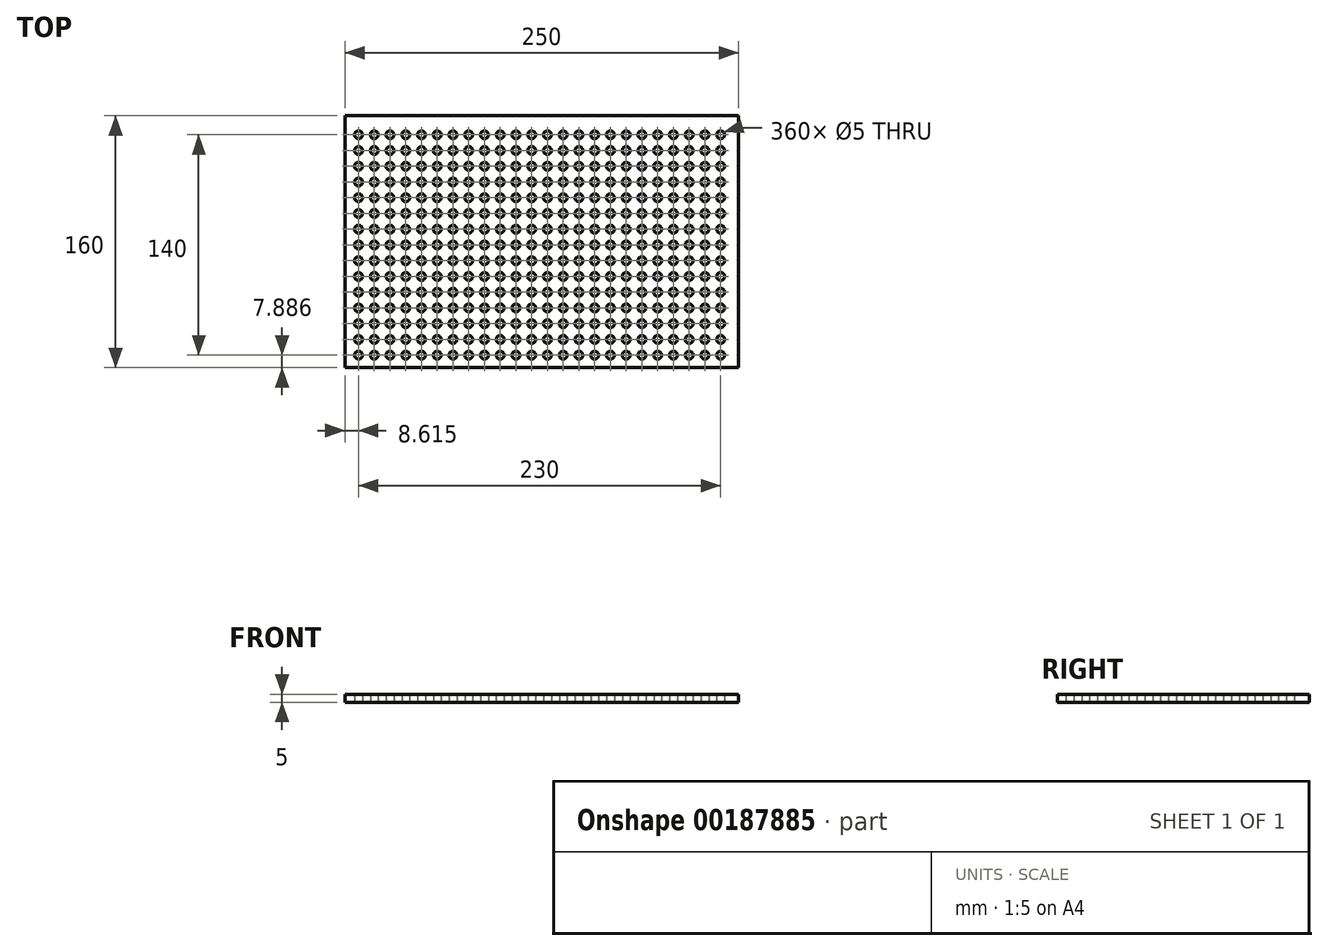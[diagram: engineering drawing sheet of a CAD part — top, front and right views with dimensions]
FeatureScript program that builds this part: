
annotation { "Feature Type Name" : "Feature", "Feature Type Description" : "" }
export const myFeature = defineFeature(function(context is Context, id is Id, definition is map)
    precondition{}
    {
        {
            var Q0;
            Q0=qCreatedBy(makeId("Top.planeOp"),FACE);
            var sketch = newSketch(context, id + "F0", { "sketchPlane" : qUnion([Q0])});
            skLineSegment(sketch, "E0.bottom", {"start": v(125, -80) * mm, "end": v(-125, -80) * mm});
            skLineSegment(sketch, "E0.top", {"start": v(125, 80) * mm, "end": v(-125, 80) * mm});
            skLineSegment(sketch, "E0.left", {"start": v(125, -80) * mm, "end": v(125, 80) * mm});
            skLineSegment(sketch, "E0.right", {"start": v(-125, -80) * mm, "end": v(-125, 80) * mm});
            skPoint(sketch, "E0.middle", {"position": v(0, 0) * mm});
            skCircle(sketch, "E1", {"center": v(-116.38, -72.11) * mm, "radius": 2.5 * mm});
            skCircle(sketch, "E2.0.1.0", {"center": v(-116.38, -62.11) * mm, "radius": 2.5 * mm});
            skCircle(sketch, "E2.0.2.0", {"center": v(-116.38, -52.11) * mm, "radius": 2.5 * mm});
            skCircle(sketch, "E2.0.3.0", {"center": v(-116.38, -42.11) * mm, "radius": 2.5 * mm});
            skCircle(sketch, "E2.0.4.0", {"center": v(-116.38, -32.11) * mm, "radius": 2.5 * mm});
            skCircle(sketch, "E2.0.5.0", {"center": v(-116.38, -22.11) * mm, "radius": 2.5 * mm});
            skCircle(sketch, "E2.0.6.0", {"center": v(-116.38, -12.11) * mm, "radius": 2.5 * mm});
            skCircle(sketch, "E2.0.7.0", {"center": v(-116.38, -2.11) * mm, "radius": 2.5 * mm});
            skCircle(sketch, "E2.0.8.0", {"center": v(-116.38, 7.89) * mm, "radius": 2.5 * mm});
            skCircle(sketch, "E2.0.9.0", {"center": v(-116.38, 17.89) * mm, "radius": 2.5 * mm});
            skCircle(sketch, "E2.0.10.0", {"center": v(-116.38, 27.89) * mm, "radius": 2.5 * mm});
            skCircle(sketch, "E2.0.11.0", {"center": v(-116.38, 37.89) * mm, "radius": 2.5 * mm});
            skCircle(sketch, "E2.0.12.0", {"center": v(-116.38, 47.89) * mm, "radius": 2.5 * mm});
            skCircle(sketch, "E2.0.13.0", {"center": v(-116.38, 57.89) * mm, "radius": 2.5 * mm});
            skCircle(sketch, "E2.0.14.0", {"center": v(-116.38, 67.89) * mm, "radius": 2.5 * mm});
            skCircle(sketch, "E2.1.0.0", {"center": v(-106.38, -72.11) * mm, "radius": 2.5 * mm});
            skCircle(sketch, "E2.1.1.0", {"center": v(-106.38, -62.11) * mm, "radius": 2.5 * mm});
            skCircle(sketch, "E2.1.2.0", {"center": v(-106.38, -52.11) * mm, "radius": 2.5 * mm});
            skCircle(sketch, "E2.1.3.0", {"center": v(-106.38, -42.11) * mm, "radius": 2.5 * mm});
            skCircle(sketch, "E2.1.4.0", {"center": v(-106.38, -32.11) * mm, "radius": 2.5 * mm});
            skCircle(sketch, "E2.1.5.0", {"center": v(-106.38, -22.11) * mm, "radius": 2.5 * mm});
            skCircle(sketch, "E2.1.6.0", {"center": v(-106.38, -12.11) * mm, "radius": 2.5 * mm});
            skCircle(sketch, "E2.1.7.0", {"center": v(-106.38, -2.11) * mm, "radius": 2.5 * mm});
            skCircle(sketch, "E2.1.8.0", {"center": v(-106.38, 7.89) * mm, "radius": 2.5 * mm});
            skCircle(sketch, "E2.1.9.0", {"center": v(-106.38, 17.89) * mm, "radius": 2.5 * mm});
            skCircle(sketch, "E2.1.10.0", {"center": v(-106.38, 27.89) * mm, "radius": 2.5 * mm});
            skCircle(sketch, "E2.1.11.0", {"center": v(-106.38, 37.89) * mm, "radius": 2.5 * mm});
            skCircle(sketch, "E2.1.12.0", {"center": v(-106.38, 47.89) * mm, "radius": 2.5 * mm});
            skCircle(sketch, "E2.1.13.0", {"center": v(-106.38, 57.89) * mm, "radius": 2.5 * mm});
            skCircle(sketch, "E2.1.14.0", {"center": v(-106.38, 67.89) * mm, "radius": 2.5 * mm});
            skCircle(sketch, "E2.2.0.0", {"center": v(-96.38, -72.11) * mm, "radius": 2.5 * mm});
            skCircle(sketch, "E2.2.1.0", {"center": v(-96.38, -62.11) * mm, "radius": 2.5 * mm});
            skCircle(sketch, "E2.2.2.0", {"center": v(-96.38, -52.11) * mm, "radius": 2.5 * mm});
            skCircle(sketch, "E2.2.3.0", {"center": v(-96.38, -42.11) * mm, "radius": 2.5 * mm});
            skCircle(sketch, "E2.2.4.0", {"center": v(-96.38, -32.11) * mm, "radius": 2.5 * mm});
            skCircle(sketch, "E2.2.5.0", {"center": v(-96.38, -22.11) * mm, "radius": 2.5 * mm});
            skCircle(sketch, "E2.2.6.0", {"center": v(-96.38, -12.11) * mm, "radius": 2.5 * mm});
            skCircle(sketch, "E2.2.7.0", {"center": v(-96.38, -2.11) * mm, "radius": 2.5 * mm});
            skCircle(sketch, "E2.2.8.0", {"center": v(-96.38, 7.89) * mm, "radius": 2.5 * mm});
            skCircle(sketch, "E2.2.9.0", {"center": v(-96.38, 17.89) * mm, "radius": 2.5 * mm});
            skCircle(sketch, "E2.2.10.0", {"center": v(-96.38, 27.89) * mm, "radius": 2.5 * mm});
            skCircle(sketch, "E2.2.11.0", {"center": v(-96.38, 37.89) * mm, "radius": 2.5 * mm});
            skCircle(sketch, "E2.2.12.0", {"center": v(-96.38, 47.89) * mm, "radius": 2.5 * mm});
            skCircle(sketch, "E2.2.13.0", {"center": v(-96.38, 57.89) * mm, "radius": 2.5 * mm});
            skCircle(sketch, "E2.2.14.0", {"center": v(-96.38, 67.89) * mm, "radius": 2.5 * mm});
            skCircle(sketch, "E2.3.0.0", {"center": v(-86.38, -72.11) * mm, "radius": 2.5 * mm});
            skCircle(sketch, "E2.3.1.0", {"center": v(-86.38, -62.11) * mm, "radius": 2.5 * mm});
            skCircle(sketch, "E2.3.2.0", {"center": v(-86.38, -52.11) * mm, "radius": 2.5 * mm});
            skCircle(sketch, "E2.3.3.0", {"center": v(-86.38, -42.11) * mm, "radius": 2.5 * mm});
            skCircle(sketch, "E2.3.4.0", {"center": v(-86.38, -32.11) * mm, "radius": 2.5 * mm});
            skCircle(sketch, "E2.3.5.0", {"center": v(-86.38, -22.11) * mm, "radius": 2.5 * mm});
            skCircle(sketch, "E2.3.6.0", {"center": v(-86.38, -12.11) * mm, "radius": 2.5 * mm});
            skCircle(sketch, "E2.3.7.0", {"center": v(-86.38, -2.11) * mm, "radius": 2.5 * mm});
            skCircle(sketch, "E2.3.8.0", {"center": v(-86.38, 7.89) * mm, "radius": 2.5 * mm});
            skCircle(sketch, "E2.3.9.0", {"center": v(-86.38, 17.89) * mm, "radius": 2.5 * mm});
            skCircle(sketch, "E2.3.10.0", {"center": v(-86.38, 27.89) * mm, "radius": 2.5 * mm});
            skCircle(sketch, "E2.3.11.0", {"center": v(-86.38, 37.89) * mm, "radius": 2.5 * mm});
            skCircle(sketch, "E2.3.12.0", {"center": v(-86.38, 47.89) * mm, "radius": 2.5 * mm});
            skCircle(sketch, "E2.3.13.0", {"center": v(-86.38, 57.89) * mm, "radius": 2.5 * mm});
            skCircle(sketch, "E2.3.14.0", {"center": v(-86.38, 67.89) * mm, "radius": 2.5 * mm});
            skCircle(sketch, "E2.4.0.0", {"center": v(-76.38, -72.11) * mm, "radius": 2.5 * mm});
            skCircle(sketch, "E2.4.1.0", {"center": v(-76.38, -62.11) * mm, "radius": 2.5 * mm});
            skCircle(sketch, "E2.4.2.0", {"center": v(-76.38, -52.11) * mm, "radius": 2.5 * mm});
            skCircle(sketch, "E2.4.3.0", {"center": v(-76.38, -42.11) * mm, "radius": 2.5 * mm});
            skCircle(sketch, "E2.4.4.0", {"center": v(-76.38, -32.11) * mm, "radius": 2.5 * mm});
            skCircle(sketch, "E2.4.5.0", {"center": v(-76.38, -22.11) * mm, "radius": 2.5 * mm});
            skCircle(sketch, "E2.4.6.0", {"center": v(-76.38, -12.11) * mm, "radius": 2.5 * mm});
            skCircle(sketch, "E2.4.7.0", {"center": v(-76.38, -2.11) * mm, "radius": 2.5 * mm});
            skCircle(sketch, "E2.4.8.0", {"center": v(-76.38, 7.89) * mm, "radius": 2.5 * mm});
            skCircle(sketch, "E2.4.9.0", {"center": v(-76.38, 17.89) * mm, "radius": 2.5 * mm});
            skCircle(sketch, "E2.4.10.0", {"center": v(-76.38, 27.89) * mm, "radius": 2.5 * mm});
            skCircle(sketch, "E2.4.11.0", {"center": v(-76.38, 37.89) * mm, "radius": 2.5 * mm});
            skCircle(sketch, "E2.4.12.0", {"center": v(-76.38, 47.89) * mm, "radius": 2.5 * mm});
            skCircle(sketch, "E2.4.13.0", {"center": v(-76.38, 57.89) * mm, "radius": 2.5 * mm});
            skCircle(sketch, "E2.4.14.0", {"center": v(-76.38, 67.89) * mm, "radius": 2.5 * mm});
            skCircle(sketch, "E2.5.0.0", {"center": v(-66.38, -72.11) * mm, "radius": 2.5 * mm});
            skCircle(sketch, "E2.5.1.0", {"center": v(-66.38, -62.11) * mm, "radius": 2.5 * mm});
            skCircle(sketch, "E2.5.2.0", {"center": v(-66.38, -52.11) * mm, "radius": 2.5 * mm});
            skCircle(sketch, "E2.5.3.0", {"center": v(-66.38, -42.11) * mm, "radius": 2.5 * mm});
            skCircle(sketch, "E2.5.4.0", {"center": v(-66.38, -32.11) * mm, "radius": 2.5 * mm});
            skCircle(sketch, "E2.5.5.0", {"center": v(-66.38, -22.11) * mm, "radius": 2.5 * mm});
            skCircle(sketch, "E2.5.6.0", {"center": v(-66.38, -12.11) * mm, "radius": 2.5 * mm});
            skCircle(sketch, "E2.5.7.0", {"center": v(-66.38, -2.11) * mm, "radius": 2.5 * mm});
            skCircle(sketch, "E2.5.8.0", {"center": v(-66.38, 7.89) * mm, "radius": 2.5 * mm});
            skCircle(sketch, "E2.5.9.0", {"center": v(-66.38, 17.89) * mm, "radius": 2.5 * mm});
            skCircle(sketch, "E2.5.10.0", {"center": v(-66.38, 27.89) * mm, "radius": 2.5 * mm});
            skCircle(sketch, "E2.5.11.0", {"center": v(-66.38, 37.89) * mm, "radius": 2.5 * mm});
            skCircle(sketch, "E2.5.12.0", {"center": v(-66.38, 47.89) * mm, "radius": 2.5 * mm});
            skCircle(sketch, "E2.5.13.0", {"center": v(-66.38, 57.89) * mm, "radius": 2.5 * mm});
            skCircle(sketch, "E2.5.14.0", {"center": v(-66.38, 67.89) * mm, "radius": 2.5 * mm});
            skCircle(sketch, "E2.6.0.0", {"center": v(-56.38, -72.11) * mm, "radius": 2.5 * mm});
            skCircle(sketch, "E2.6.1.0", {"center": v(-56.38, -62.11) * mm, "radius": 2.5 * mm});
            skCircle(sketch, "E2.6.2.0", {"center": v(-56.38, -52.11) * mm, "radius": 2.5 * mm});
            skCircle(sketch, "E2.6.3.0", {"center": v(-56.38, -42.11) * mm, "radius": 2.5 * mm});
            skCircle(sketch, "E2.6.4.0", {"center": v(-56.38, -32.11) * mm, "radius": 2.5 * mm});
            skCircle(sketch, "E2.6.5.0", {"center": v(-56.38, -22.11) * mm, "radius": 2.5 * mm});
            skCircle(sketch, "E2.6.6.0", {"center": v(-56.38, -12.11) * mm, "radius": 2.5 * mm});
            skCircle(sketch, "E2.6.7.0", {"center": v(-56.38, -2.11) * mm, "radius": 2.5 * mm});
            skCircle(sketch, "E2.6.8.0", {"center": v(-56.38, 7.89) * mm, "radius": 2.5 * mm});
            skCircle(sketch, "E2.6.9.0", {"center": v(-56.38, 17.89) * mm, "radius": 2.5 * mm});
            skCircle(sketch, "E2.6.10.0", {"center": v(-56.38, 27.89) * mm, "radius": 2.5 * mm});
            skCircle(sketch, "E2.6.11.0", {"center": v(-56.38, 37.89) * mm, "radius": 2.5 * mm});
            skCircle(sketch, "E2.6.12.0", {"center": v(-56.38, 47.89) * mm, "radius": 2.5 * mm});
            skCircle(sketch, "E2.6.13.0", {"center": v(-56.38, 57.89) * mm, "radius": 2.5 * mm});
            skCircle(sketch, "E2.6.14.0", {"center": v(-56.38, 67.89) * mm, "radius": 2.5 * mm});
            skCircle(sketch, "E2.7.0.0", {"center": v(-46.38, -72.11) * mm, "radius": 2.5 * mm});
            skCircle(sketch, "E2.7.1.0", {"center": v(-46.38, -62.11) * mm, "radius": 2.5 * mm});
            skCircle(sketch, "E2.7.2.0", {"center": v(-46.38, -52.11) * mm, "radius": 2.5 * mm});
            skCircle(sketch, "E2.7.3.0", {"center": v(-46.38, -42.11) * mm, "radius": 2.5 * mm});
            skCircle(sketch, "E2.7.4.0", {"center": v(-46.38, -32.11) * mm, "radius": 2.5 * mm});
            skCircle(sketch, "E2.7.5.0", {"center": v(-46.38, -22.11) * mm, "radius": 2.5 * mm});
            skCircle(sketch, "E2.7.6.0", {"center": v(-46.38, -12.11) * mm, "radius": 2.5 * mm});
            skCircle(sketch, "E2.7.7.0", {"center": v(-46.38, -2.11) * mm, "radius": 2.5 * mm});
            skCircle(sketch, "E2.7.8.0", {"center": v(-46.38, 7.89) * mm, "radius": 2.5 * mm});
            skCircle(sketch, "E2.7.9.0", {"center": v(-46.38, 17.89) * mm, "radius": 2.5 * mm});
            skCircle(sketch, "E2.7.10.0", {"center": v(-46.38, 27.89) * mm, "radius": 2.5 * mm});
            skCircle(sketch, "E2.7.11.0", {"center": v(-46.38, 37.89) * mm, "radius": 2.5 * mm});
            skCircle(sketch, "E2.7.12.0", {"center": v(-46.38, 47.89) * mm, "radius": 2.5 * mm});
            skCircle(sketch, "E2.7.13.0", {"center": v(-46.38, 57.89) * mm, "radius": 2.5 * mm});
            skCircle(sketch, "E2.7.14.0", {"center": v(-46.38, 67.89) * mm, "radius": 2.5 * mm});
            skCircle(sketch, "E2.8.0.0", {"center": v(-36.38, -72.11) * mm, "radius": 2.5 * mm});
            skCircle(sketch, "E2.8.1.0", {"center": v(-36.38, -62.11) * mm, "radius": 2.5 * mm});
            skCircle(sketch, "E2.8.2.0", {"center": v(-36.38, -52.11) * mm, "radius": 2.5 * mm});
            skCircle(sketch, "E2.8.3.0", {"center": v(-36.38, -42.11) * mm, "radius": 2.5 * mm});
            skCircle(sketch, "E2.8.4.0", {"center": v(-36.38, -32.11) * mm, "radius": 2.5 * mm});
            skCircle(sketch, "E2.8.5.0", {"center": v(-36.38, -22.11) * mm, "radius": 2.5 * mm});
            skCircle(sketch, "E2.8.6.0", {"center": v(-36.38, -12.11) * mm, "radius": 2.5 * mm});
            skCircle(sketch, "E2.8.7.0", {"center": v(-36.38, -2.11) * mm, "radius": 2.5 * mm});
            skCircle(sketch, "E2.8.8.0", {"center": v(-36.38, 7.89) * mm, "radius": 2.5 * mm});
            skCircle(sketch, "E2.8.9.0", {"center": v(-36.38, 17.89) * mm, "radius": 2.5 * mm});
            skCircle(sketch, "E2.8.10.0", {"center": v(-36.38, 27.89) * mm, "radius": 2.5 * mm});
            skCircle(sketch, "E2.8.11.0", {"center": v(-36.38, 37.89) * mm, "radius": 2.5 * mm});
            skCircle(sketch, "E2.8.12.0", {"center": v(-36.38, 47.89) * mm, "radius": 2.5 * mm});
            skCircle(sketch, "E2.8.13.0", {"center": v(-36.38, 57.89) * mm, "radius": 2.5 * mm});
            skCircle(sketch, "E2.8.14.0", {"center": v(-36.38, 67.89) * mm, "radius": 2.5 * mm});
            skCircle(sketch, "E2.9.0.0", {"center": v(-26.38, -72.11) * mm, "radius": 2.5 * mm});
            skCircle(sketch, "E2.9.1.0", {"center": v(-26.38, -62.11) * mm, "radius": 2.5 * mm});
            skCircle(sketch, "E2.9.2.0", {"center": v(-26.38, -52.11) * mm, "radius": 2.5 * mm});
            skCircle(sketch, "E2.9.3.0", {"center": v(-26.38, -42.11) * mm, "radius": 2.5 * mm});
            skCircle(sketch, "E2.9.4.0", {"center": v(-26.38, -32.11) * mm, "radius": 2.5 * mm});
            skCircle(sketch, "E2.9.5.0", {"center": v(-26.38, -22.11) * mm, "radius": 2.5 * mm});
            skCircle(sketch, "E2.9.6.0", {"center": v(-26.38, -12.11) * mm, "radius": 2.5 * mm});
            skCircle(sketch, "E2.9.7.0", {"center": v(-26.38, -2.11) * mm, "radius": 2.5 * mm});
            skCircle(sketch, "E2.9.8.0", {"center": v(-26.38, 7.89) * mm, "radius": 2.5 * mm});
            skCircle(sketch, "E2.9.9.0", {"center": v(-26.38, 17.89) * mm, "radius": 2.5 * mm});
            skCircle(sketch, "E2.9.10.0", {"center": v(-26.38, 27.89) * mm, "radius": 2.5 * mm});
            skCircle(sketch, "E2.9.11.0", {"center": v(-26.38, 37.89) * mm, "radius": 2.5 * mm});
            skCircle(sketch, "E2.9.12.0", {"center": v(-26.38, 47.89) * mm, "radius": 2.5 * mm});
            skCircle(sketch, "E2.9.13.0", {"center": v(-26.38, 57.89) * mm, "radius": 2.5 * mm});
            skCircle(sketch, "E2.9.14.0", {"center": v(-26.38, 67.89) * mm, "radius": 2.5 * mm});
            skCircle(sketch, "E2.10.0.0", {"center": v(-16.38, -72.11) * mm, "radius": 2.5 * mm});
            skCircle(sketch, "E2.10.1.0", {"center": v(-16.38, -62.11) * mm, "radius": 2.5 * mm});
            skCircle(sketch, "E2.10.2.0", {"center": v(-16.38, -52.11) * mm, "radius": 2.5 * mm});
            skCircle(sketch, "E2.10.3.0", {"center": v(-16.38, -42.11) * mm, "radius": 2.5 * mm});
            skCircle(sketch, "E2.10.4.0", {"center": v(-16.38, -32.11) * mm, "radius": 2.5 * mm});
            skCircle(sketch, "E2.10.5.0", {"center": v(-16.38, -22.11) * mm, "radius": 2.5 * mm});
            skCircle(sketch, "E2.10.6.0", {"center": v(-16.38, -12.11) * mm, "radius": 2.5 * mm});
            skCircle(sketch, "E2.10.7.0", {"center": v(-16.38, -2.11) * mm, "radius": 2.5 * mm});
            skCircle(sketch, "E2.10.8.0", {"center": v(-16.38, 7.89) * mm, "radius": 2.5 * mm});
            skCircle(sketch, "E2.10.9.0", {"center": v(-16.38, 17.89) * mm, "radius": 2.5 * mm});
            skCircle(sketch, "E2.10.10.0", {"center": v(-16.38, 27.89) * mm, "radius": 2.5 * mm});
            skCircle(sketch, "E2.10.11.0", {"center": v(-16.38, 37.89) * mm, "radius": 2.5 * mm});
            skCircle(sketch, "E2.10.12.0", {"center": v(-16.38, 47.89) * mm, "radius": 2.5 * mm});
            skCircle(sketch, "E2.10.13.0", {"center": v(-16.38, 57.89) * mm, "radius": 2.5 * mm});
            skCircle(sketch, "E2.10.14.0", {"center": v(-16.38, 67.89) * mm, "radius": 2.5 * mm});
            skCircle(sketch, "E2.11.0.0", {"center": v(-6.38, -72.11) * mm, "radius": 2.5 * mm});
            skCircle(sketch, "E2.11.1.0", {"center": v(-6.38, -62.11) * mm, "radius": 2.5 * mm});
            skCircle(sketch, "E2.11.2.0", {"center": v(-6.38, -52.11) * mm, "radius": 2.5 * mm});
            skCircle(sketch, "E2.11.3.0", {"center": v(-6.38, -42.11) * mm, "radius": 2.5 * mm});
            skCircle(sketch, "E2.11.4.0", {"center": v(-6.38, -32.11) * mm, "radius": 2.5 * mm});
            skCircle(sketch, "E2.11.5.0", {"center": v(-6.38, -22.11) * mm, "radius": 2.5 * mm});
            skCircle(sketch, "E2.11.6.0", {"center": v(-6.38, -12.11) * mm, "radius": 2.5 * mm});
            skCircle(sketch, "E2.11.7.0", {"center": v(-6.38, -2.11) * mm, "radius": 2.5 * mm});
            skCircle(sketch, "E2.11.8.0", {"center": v(-6.38, 7.89) * mm, "radius": 2.5 * mm});
            skCircle(sketch, "E2.11.9.0", {"center": v(-6.38, 17.89) * mm, "radius": 2.5 * mm});
            skCircle(sketch, "E2.11.10.0", {"center": v(-6.38, 27.89) * mm, "radius": 2.5 * mm});
            skCircle(sketch, "E2.11.11.0", {"center": v(-6.38, 37.89) * mm, "radius": 2.5 * mm});
            skCircle(sketch, "E2.11.12.0", {"center": v(-6.38, 47.89) * mm, "radius": 2.5 * mm});
            skCircle(sketch, "E2.11.13.0", {"center": v(-6.38, 57.89) * mm, "radius": 2.5 * mm});
            skCircle(sketch, "E2.11.14.0", {"center": v(-6.38, 67.89) * mm, "radius": 2.5 * mm});
            skCircle(sketch, "E2.12.0.0", {"center": v(3.62, -72.11) * mm, "radius": 2.5 * mm});
            skCircle(sketch, "E2.12.1.0", {"center": v(3.62, -62.11) * mm, "radius": 2.5 * mm});
            skCircle(sketch, "E2.12.2.0", {"center": v(3.62, -52.11) * mm, "radius": 2.5 * mm});
            skCircle(sketch, "E2.12.3.0", {"center": v(3.62, -42.11) * mm, "radius": 2.5 * mm});
            skCircle(sketch, "E2.12.4.0", {"center": v(3.62, -32.11) * mm, "radius": 2.5 * mm});
            skCircle(sketch, "E2.12.5.0", {"center": v(3.62, -22.11) * mm, "radius": 2.5 * mm});
            skCircle(sketch, "E2.12.6.0", {"center": v(3.62, -12.11) * mm, "radius": 2.5 * mm});
            skCircle(sketch, "E2.12.7.0", {"center": v(3.62, -2.11) * mm, "radius": 2.5 * mm});
            skCircle(sketch, "E2.12.8.0", {"center": v(3.62, 7.89) * mm, "radius": 2.5 * mm});
            skCircle(sketch, "E2.12.9.0", {"center": v(3.62, 17.89) * mm, "radius": 2.5 * mm});
            skCircle(sketch, "E2.12.10.0", {"center": v(3.62, 27.89) * mm, "radius": 2.5 * mm});
            skCircle(sketch, "E2.12.11.0", {"center": v(3.62, 37.89) * mm, "radius": 2.5 * mm});
            skCircle(sketch, "E2.12.12.0", {"center": v(3.62, 47.89) * mm, "radius": 2.5 * mm});
            skCircle(sketch, "E2.12.13.0", {"center": v(3.62, 57.89) * mm, "radius": 2.5 * mm});
            skCircle(sketch, "E2.12.14.0", {"center": v(3.62, 67.89) * mm, "radius": 2.5 * mm});
            skCircle(sketch, "E2.13.0.0", {"center": v(13.62, -72.11) * mm, "radius": 2.5 * mm});
            skCircle(sketch, "E2.13.1.0", {"center": v(13.62, -62.11) * mm, "radius": 2.5 * mm});
            skCircle(sketch, "E2.13.2.0", {"center": v(13.62, -52.11) * mm, "radius": 2.5 * mm});
            skCircle(sketch, "E2.13.3.0", {"center": v(13.62, -42.11) * mm, "radius": 2.5 * mm});
            skCircle(sketch, "E2.13.4.0", {"center": v(13.62, -32.11) * mm, "radius": 2.5 * mm});
            skCircle(sketch, "E2.13.5.0", {"center": v(13.62, -22.11) * mm, "radius": 2.5 * mm});
            skCircle(sketch, "E2.13.6.0", {"center": v(13.62, -12.11) * mm, "radius": 2.5 * mm});
            skCircle(sketch, "E2.13.7.0", {"center": v(13.62, -2.11) * mm, "radius": 2.5 * mm});
            skCircle(sketch, "E2.13.8.0", {"center": v(13.62, 7.89) * mm, "radius": 2.5 * mm});
            skCircle(sketch, "E2.13.9.0", {"center": v(13.62, 17.89) * mm, "radius": 2.5 * mm});
            skCircle(sketch, "E2.13.10.0", {"center": v(13.62, 27.89) * mm, "radius": 2.5 * mm});
            skCircle(sketch, "E2.13.11.0", {"center": v(13.62, 37.89) * mm, "radius": 2.5 * mm});
            skCircle(sketch, "E2.13.12.0", {"center": v(13.62, 47.89) * mm, "radius": 2.5 * mm});
            skCircle(sketch, "E2.13.13.0", {"center": v(13.62, 57.89) * mm, "radius": 2.5 * mm});
            skCircle(sketch, "E2.13.14.0", {"center": v(13.62, 67.89) * mm, "radius": 2.5 * mm});
            skCircle(sketch, "E2.14.0.0", {"center": v(23.62, -72.11) * mm, "radius": 2.5 * mm});
            skCircle(sketch, "E2.14.1.0", {"center": v(23.62, -62.11) * mm, "radius": 2.5 * mm});
            skCircle(sketch, "E2.14.2.0", {"center": v(23.62, -52.11) * mm, "radius": 2.5 * mm});
            skCircle(sketch, "E2.14.3.0", {"center": v(23.62, -42.11) * mm, "radius": 2.5 * mm});
            skCircle(sketch, "E2.14.4.0", {"center": v(23.62, -32.11) * mm, "radius": 2.5 * mm});
            skCircle(sketch, "E2.14.5.0", {"center": v(23.62, -22.11) * mm, "radius": 2.5 * mm});
            skCircle(sketch, "E2.14.6.0", {"center": v(23.62, -12.11) * mm, "radius": 2.5 * mm});
            skCircle(sketch, "E2.14.7.0", {"center": v(23.62, -2.11) * mm, "radius": 2.5 * mm});
            skCircle(sketch, "E2.14.8.0", {"center": v(23.62, 7.89) * mm, "radius": 2.5 * mm});
            skCircle(sketch, "E2.14.9.0", {"center": v(23.62, 17.89) * mm, "radius": 2.5 * mm});
            skCircle(sketch, "E2.14.10.0", {"center": v(23.62, 27.89) * mm, "radius": 2.5 * mm});
            skCircle(sketch, "E2.14.11.0", {"center": v(23.62, 37.89) * mm, "radius": 2.5 * mm});
            skCircle(sketch, "E2.14.12.0", {"center": v(23.62, 47.89) * mm, "radius": 2.5 * mm});
            skCircle(sketch, "E2.14.13.0", {"center": v(23.62, 57.89) * mm, "radius": 2.5 * mm});
            skCircle(sketch, "E2.14.14.0", {"center": v(23.62, 67.89) * mm, "radius": 2.5 * mm});
            skCircle(sketch, "E2.15.0.0", {"center": v(33.62, -72.11) * mm, "radius": 2.5 * mm});
            skCircle(sketch, "E2.15.1.0", {"center": v(33.62, -62.11) * mm, "radius": 2.5 * mm});
            skCircle(sketch, "E2.15.2.0", {"center": v(33.62, -52.11) * mm, "radius": 2.5 * mm});
            skCircle(sketch, "E2.15.3.0", {"center": v(33.62, -42.11) * mm, "radius": 2.5 * mm});
            skCircle(sketch, "E2.15.4.0", {"center": v(33.62, -32.11) * mm, "radius": 2.5 * mm});
            skCircle(sketch, "E2.15.5.0", {"center": v(33.62, -22.11) * mm, "radius": 2.5 * mm});
            skCircle(sketch, "E2.15.6.0", {"center": v(33.62, -12.11) * mm, "radius": 2.5 * mm});
            skCircle(sketch, "E2.15.7.0", {"center": v(33.62, -2.11) * mm, "radius": 2.5 * mm});
            skCircle(sketch, "E2.15.8.0", {"center": v(33.62, 7.89) * mm, "radius": 2.5 * mm});
            skCircle(sketch, "E2.15.9.0", {"center": v(33.62, 17.89) * mm, "radius": 2.5 * mm});
            skCircle(sketch, "E2.15.10.0", {"center": v(33.62, 27.89) * mm, "radius": 2.5 * mm});
            skCircle(sketch, "E2.15.11.0", {"center": v(33.62, 37.89) * mm, "radius": 2.5 * mm});
            skCircle(sketch, "E2.15.12.0", {"center": v(33.62, 47.89) * mm, "radius": 2.5 * mm});
            skCircle(sketch, "E2.15.13.0", {"center": v(33.62, 57.89) * mm, "radius": 2.5 * mm});
            skCircle(sketch, "E2.15.14.0", {"center": v(33.62, 67.89) * mm, "radius": 2.5 * mm});
            skCircle(sketch, "E2.16.0.0", {"center": v(43.62, -72.11) * mm, "radius": 2.5 * mm});
            skCircle(sketch, "E2.16.1.0", {"center": v(43.62, -62.11) * mm, "radius": 2.5 * mm});
            skCircle(sketch, "E2.16.2.0", {"center": v(43.62, -52.11) * mm, "radius": 2.5 * mm});
            skCircle(sketch, "E2.16.3.0", {"center": v(43.62, -42.11) * mm, "radius": 2.5 * mm});
            skCircle(sketch, "E2.16.4.0", {"center": v(43.62, -32.11) * mm, "radius": 2.5 * mm});
            skCircle(sketch, "E2.16.5.0", {"center": v(43.62, -22.11) * mm, "radius": 2.5 * mm});
            skCircle(sketch, "E2.16.6.0", {"center": v(43.62, -12.11) * mm, "radius": 2.5 * mm});
            skCircle(sketch, "E2.16.7.0", {"center": v(43.62, -2.11) * mm, "radius": 2.5 * mm});
            skCircle(sketch, "E2.16.8.0", {"center": v(43.62, 7.89) * mm, "radius": 2.5 * mm});
            skCircle(sketch, "E2.16.9.0", {"center": v(43.62, 17.89) * mm, "radius": 2.5 * mm});
            skCircle(sketch, "E2.16.10.0", {"center": v(43.62, 27.89) * mm, "radius": 2.5 * mm});
            skCircle(sketch, "E2.16.11.0", {"center": v(43.62, 37.89) * mm, "radius": 2.5 * mm});
            skCircle(sketch, "E2.16.12.0", {"center": v(43.62, 47.89) * mm, "radius": 2.5 * mm});
            skCircle(sketch, "E2.16.13.0", {"center": v(43.62, 57.89) * mm, "radius": 2.5 * mm});
            skCircle(sketch, "E2.16.14.0", {"center": v(43.62, 67.89) * mm, "radius": 2.5 * mm});
            skCircle(sketch, "E2.17.0.0", {"center": v(53.62, -72.11) * mm, "radius": 2.5 * mm});
            skCircle(sketch, "E2.17.1.0", {"center": v(53.62, -62.11) * mm, "radius": 2.5 * mm});
            skCircle(sketch, "E2.17.2.0", {"center": v(53.62, -52.11) * mm, "radius": 2.5 * mm});
            skCircle(sketch, "E2.17.3.0", {"center": v(53.62, -42.11) * mm, "radius": 2.5 * mm});
            skCircle(sketch, "E2.17.4.0", {"center": v(53.62, -32.11) * mm, "radius": 2.5 * mm});
            skCircle(sketch, "E2.17.5.0", {"center": v(53.62, -22.11) * mm, "radius": 2.5 * mm});
            skCircle(sketch, "E2.17.6.0", {"center": v(53.62, -12.11) * mm, "radius": 2.5 * mm});
            skCircle(sketch, "E2.17.7.0", {"center": v(53.62, -2.11) * mm, "radius": 2.5 * mm});
            skCircle(sketch, "E2.17.8.0", {"center": v(53.62, 7.89) * mm, "radius": 2.5 * mm});
            skCircle(sketch, "E2.17.9.0", {"center": v(53.62, 17.89) * mm, "radius": 2.5 * mm});
            skCircle(sketch, "E2.17.10.0", {"center": v(53.62, 27.89) * mm, "radius": 2.5 * mm});
            skCircle(sketch, "E2.17.11.0", {"center": v(53.62, 37.89) * mm, "radius": 2.5 * mm});
            skCircle(sketch, "E2.17.12.0", {"center": v(53.62, 47.89) * mm, "radius": 2.5 * mm});
            skCircle(sketch, "E2.17.13.0", {"center": v(53.62, 57.89) * mm, "radius": 2.5 * mm});
            skCircle(sketch, "E2.17.14.0", {"center": v(53.62, 67.89) * mm, "radius": 2.5 * mm});
            skCircle(sketch, "E2.18.0.0", {"center": v(63.62, -72.11) * mm, "radius": 2.5 * mm});
            skCircle(sketch, "E2.18.1.0", {"center": v(63.62, -62.11) * mm, "radius": 2.5 * mm});
            skCircle(sketch, "E2.18.2.0", {"center": v(63.62, -52.11) * mm, "radius": 2.5 * mm});
            skCircle(sketch, "E2.18.3.0", {"center": v(63.62, -42.11) * mm, "radius": 2.5 * mm});
            skCircle(sketch, "E2.18.4.0", {"center": v(63.62, -32.11) * mm, "radius": 2.5 * mm});
            skCircle(sketch, "E2.18.5.0", {"center": v(63.62, -22.11) * mm, "radius": 2.5 * mm});
            skCircle(sketch, "E2.18.6.0", {"center": v(63.62, -12.11) * mm, "radius": 2.5 * mm});
            skCircle(sketch, "E2.18.7.0", {"center": v(63.62, -2.11) * mm, "radius": 2.5 * mm});
            skCircle(sketch, "E2.18.8.0", {"center": v(63.62, 7.89) * mm, "radius": 2.5 * mm});
            skCircle(sketch, "E2.18.9.0", {"center": v(63.62, 17.89) * mm, "radius": 2.5 * mm});
            skCircle(sketch, "E2.18.10.0", {"center": v(63.62, 27.89) * mm, "radius": 2.5 * mm});
            skCircle(sketch, "E2.18.11.0", {"center": v(63.62, 37.89) * mm, "radius": 2.5 * mm});
            skCircle(sketch, "E2.18.12.0", {"center": v(63.62, 47.89) * mm, "radius": 2.5 * mm});
            skCircle(sketch, "E2.18.13.0", {"center": v(63.62, 57.89) * mm, "radius": 2.5 * mm});
            skCircle(sketch, "E2.18.14.0", {"center": v(63.62, 67.89) * mm, "radius": 2.5 * mm});
            skCircle(sketch, "E2.19.0.0", {"center": v(73.62, -72.11) * mm, "radius": 2.5 * mm});
            skCircle(sketch, "E2.19.1.0", {"center": v(73.62, -62.11) * mm, "radius": 2.5 * mm});
            skCircle(sketch, "E2.19.2.0", {"center": v(73.62, -52.11) * mm, "radius": 2.5 * mm});
            skCircle(sketch, "E2.19.3.0", {"center": v(73.62, -42.11) * mm, "radius": 2.5 * mm});
            skCircle(sketch, "E2.19.4.0", {"center": v(73.62, -32.11) * mm, "radius": 2.5 * mm});
            skCircle(sketch, "E2.19.5.0", {"center": v(73.62, -22.11) * mm, "radius": 2.5 * mm});
            skCircle(sketch, "E2.19.6.0", {"center": v(73.62, -12.11) * mm, "radius": 2.5 * mm});
            skCircle(sketch, "E2.19.7.0", {"center": v(73.62, -2.11) * mm, "radius": 2.5 * mm});
            skCircle(sketch, "E2.19.8.0", {"center": v(73.62, 7.89) * mm, "radius": 2.5 * mm});
            skCircle(sketch, "E2.19.9.0", {"center": v(73.62, 17.89) * mm, "radius": 2.5 * mm});
            skCircle(sketch, "E2.19.10.0", {"center": v(73.62, 27.89) * mm, "radius": 2.5 * mm});
            skCircle(sketch, "E2.19.11.0", {"center": v(73.62, 37.89) * mm, "radius": 2.5 * mm});
            skCircle(sketch, "E2.19.12.0", {"center": v(73.62, 47.89) * mm, "radius": 2.5 * mm});
            skCircle(sketch, "E2.19.13.0", {"center": v(73.62, 57.89) * mm, "radius": 2.5 * mm});
            skCircle(sketch, "E2.19.14.0", {"center": v(73.62, 67.89) * mm, "radius": 2.5 * mm});
            skCircle(sketch, "E2.20.0.0", {"center": v(83.62, -72.11) * mm, "radius": 2.5 * mm});
            skCircle(sketch, "E2.20.1.0", {"center": v(83.62, -62.11) * mm, "radius": 2.5 * mm});
            skCircle(sketch, "E2.20.2.0", {"center": v(83.62, -52.11) * mm, "radius": 2.5 * mm});
            skCircle(sketch, "E2.20.3.0", {"center": v(83.62, -42.11) * mm, "radius": 2.5 * mm});
            skCircle(sketch, "E2.20.4.0", {"center": v(83.62, -32.11) * mm, "radius": 2.5 * mm});
            skCircle(sketch, "E2.20.5.0", {"center": v(83.62, -22.11) * mm, "radius": 2.5 * mm});
            skCircle(sketch, "E2.20.6.0", {"center": v(83.62, -12.11) * mm, "radius": 2.5 * mm});
            skCircle(sketch, "E2.20.7.0", {"center": v(83.62, -2.11) * mm, "radius": 2.5 * mm});
            skCircle(sketch, "E2.20.8.0", {"center": v(83.62, 7.89) * mm, "radius": 2.5 * mm});
            skCircle(sketch, "E2.20.9.0", {"center": v(83.62, 17.89) * mm, "radius": 2.5 * mm});
            skCircle(sketch, "E2.20.10.0", {"center": v(83.62, 27.89) * mm, "radius": 2.5 * mm});
            skCircle(sketch, "E2.20.11.0", {"center": v(83.62, 37.89) * mm, "radius": 2.5 * mm});
            skCircle(sketch, "E2.20.12.0", {"center": v(83.62, 47.89) * mm, "radius": 2.5 * mm});
            skCircle(sketch, "E2.20.13.0", {"center": v(83.62, 57.89) * mm, "radius": 2.5 * mm});
            skCircle(sketch, "E2.20.14.0", {"center": v(83.62, 67.89) * mm, "radius": 2.5 * mm});
            skCircle(sketch, "E2.21.0.0", {"center": v(93.62, -72.11) * mm, "radius": 2.5 * mm});
            skCircle(sketch, "E2.21.1.0", {"center": v(93.62, -62.11) * mm, "radius": 2.5 * mm});
            skCircle(sketch, "E2.21.2.0", {"center": v(93.62, -52.11) * mm, "radius": 2.5 * mm});
            skCircle(sketch, "E2.21.3.0", {"center": v(93.62, -42.11) * mm, "radius": 2.5 * mm});
            skCircle(sketch, "E2.21.4.0", {"center": v(93.62, -32.11) * mm, "radius": 2.5 * mm});
            skCircle(sketch, "E2.21.5.0", {"center": v(93.62, -22.11) * mm, "radius": 2.5 * mm});
            skCircle(sketch, "E2.21.6.0", {"center": v(93.62, -12.11) * mm, "radius": 2.5 * mm});
            skCircle(sketch, "E2.21.7.0", {"center": v(93.62, -2.11) * mm, "radius": 2.5 * mm});
            skCircle(sketch, "E2.21.8.0", {"center": v(93.62, 7.89) * mm, "radius": 2.5 * mm});
            skCircle(sketch, "E2.21.9.0", {"center": v(93.62, 17.89) * mm, "radius": 2.5 * mm});
            skCircle(sketch, "E2.21.10.0", {"center": v(93.62, 27.89) * mm, "radius": 2.5 * mm});
            skCircle(sketch, "E2.21.11.0", {"center": v(93.62, 37.89) * mm, "radius": 2.5 * mm});
            skCircle(sketch, "E2.21.12.0", {"center": v(93.62, 47.89) * mm, "radius": 2.5 * mm});
            skCircle(sketch, "E2.21.13.0", {"center": v(93.62, 57.89) * mm, "radius": 2.5 * mm});
            skCircle(sketch, "E2.21.14.0", {"center": v(93.62, 67.89) * mm, "radius": 2.5 * mm});
            skCircle(sketch, "E2.22.0.0", {"center": v(103.62, -72.11) * mm, "radius": 2.5 * mm});
            skCircle(sketch, "E2.22.1.0", {"center": v(103.62, -62.11) * mm, "radius": 2.5 * mm});
            skCircle(sketch, "E2.22.2.0", {"center": v(103.62, -52.11) * mm, "radius": 2.5 * mm});
            skCircle(sketch, "E2.22.3.0", {"center": v(103.62, -42.11) * mm, "radius": 2.5 * mm});
            skCircle(sketch, "E2.22.4.0", {"center": v(103.62, -32.11) * mm, "radius": 2.5 * mm});
            skCircle(sketch, "E2.22.5.0", {"center": v(103.62, -22.11) * mm, "radius": 2.5 * mm});
            skCircle(sketch, "E2.22.6.0", {"center": v(103.62, -12.11) * mm, "radius": 2.5 * mm});
            skCircle(sketch, "E2.22.7.0", {"center": v(103.62, -2.11) * mm, "radius": 2.5 * mm});
            skCircle(sketch, "E2.22.8.0", {"center": v(103.62, 7.89) * mm, "radius": 2.5 * mm});
            skCircle(sketch, "E2.22.9.0", {"center": v(103.62, 17.89) * mm, "radius": 2.5 * mm});
            skCircle(sketch, "E2.22.10.0", {"center": v(103.62, 27.89) * mm, "radius": 2.5 * mm});
            skCircle(sketch, "E2.22.11.0", {"center": v(103.62, 37.89) * mm, "radius": 2.5 * mm});
            skCircle(sketch, "E2.22.12.0", {"center": v(103.62, 47.89) * mm, "radius": 2.5 * mm});
            skCircle(sketch, "E2.22.13.0", {"center": v(103.62, 57.89) * mm, "radius": 2.5 * mm});
            skCircle(sketch, "E2.22.14.0", {"center": v(103.62, 67.89) * mm, "radius": 2.5 * mm});
            skCircle(sketch, "E2.23.0.0", {"center": v(113.62, -72.11) * mm, "radius": 2.5 * mm});
            skCircle(sketch, "E2.23.1.0", {"center": v(113.62, -62.11) * mm, "radius": 2.5 * mm});
            skCircle(sketch, "E2.23.2.0", {"center": v(113.62, -52.11) * mm, "radius": 2.5 * mm});
            skCircle(sketch, "E2.23.3.0", {"center": v(113.62, -42.11) * mm, "radius": 2.5 * mm});
            skCircle(sketch, "E2.23.4.0", {"center": v(113.62, -32.11) * mm, "radius": 2.5 * mm});
            skCircle(sketch, "E2.23.5.0", {"center": v(113.62, -22.11) * mm, "radius": 2.5 * mm});
            skCircle(sketch, "E2.23.6.0", {"center": v(113.62, -12.11) * mm, "radius": 2.5 * mm});
            skCircle(sketch, "E2.23.7.0", {"center": v(113.62, -2.11) * mm, "radius": 2.5 * mm});
            skCircle(sketch, "E2.23.8.0", {"center": v(113.62, 7.89) * mm, "radius": 2.5 * mm});
            skCircle(sketch, "E2.23.9.0", {"center": v(113.62, 17.89) * mm, "radius": 2.5 * mm});
            skCircle(sketch, "E2.23.10.0", {"center": v(113.62, 27.89) * mm, "radius": 2.5 * mm});
            skCircle(sketch, "E2.23.11.0", {"center": v(113.62, 37.89) * mm, "radius": 2.5 * mm});
            skCircle(sketch, "E2.23.12.0", {"center": v(113.62, 47.89) * mm, "radius": 2.5 * mm});
            skCircle(sketch, "E2.23.13.0", {"center": v(113.62, 57.89) * mm, "radius": 2.5 * mm});
            skCircle(sketch, "E2.23.14.0", {"center": v(113.62, 67.89) * mm, "radius": 2.5 * mm});
            skLineSegment(sketch, "E2.direction1", {"start": v(-116.38, -72.11) * mm, "end": v(-106.38, -72.11) * mm, "construction": true});
            skLineSegment(sketch, "E2.direction2", {"start": v(-116.38, -72.11) * mm, "end": v(-116.38, -62.11) * mm, "construction": true});
            skSolve(sketch);
        }
        {
            var Q0;
            Q0=makeQuery(id+"F0.imprint","IMPRINT",FACE,{"disambiguationData":[TD([[makeQuery(id+"F0.imprint","IMPRINT",EDGE,{"derivedFrom":sQuery(id+"F0.wireOp",EDGE,"E0.bottom")}),-1.0]])]});
            extrude(context, id + "F1", {"entities" : qUnion([Q0]), "depth" : 5 * mm});
        }
    });
